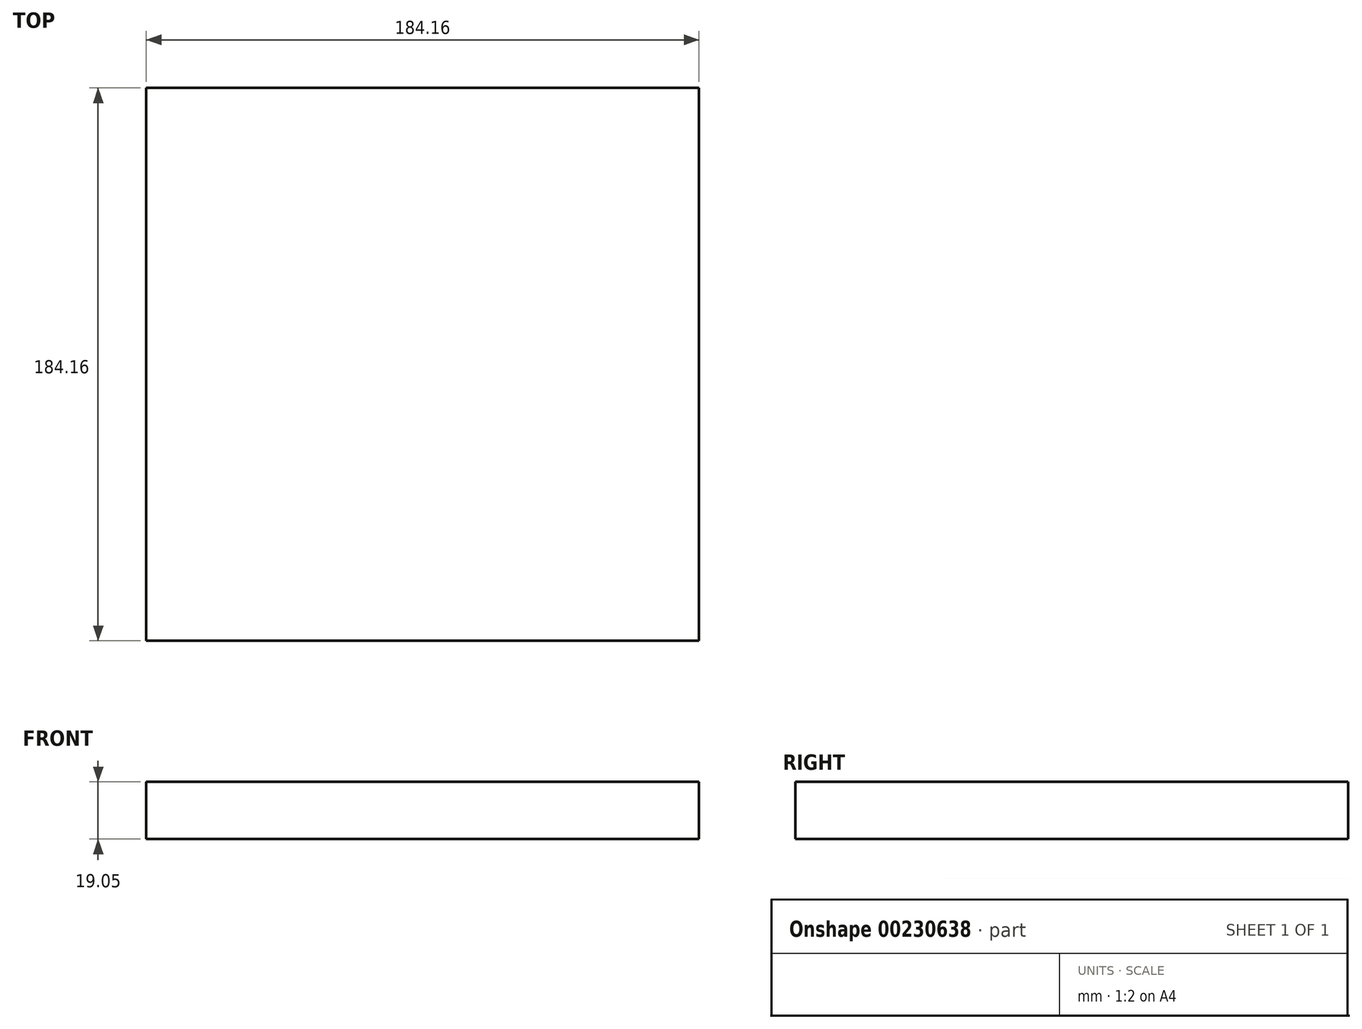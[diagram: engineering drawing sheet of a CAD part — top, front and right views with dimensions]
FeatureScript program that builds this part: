
annotation { "Feature Type Name" : "Feature", "Feature Type Description" : "" }
export const myFeature = defineFeature(function(context is Context, id is Id, definition is map)
    precondition{}
    {
        {
            var Q0;
            Q0=qCreatedBy(makeId("Top.planeOp"),FACE);
            var sketch = newSketch(context, id + "F0", { "sketchPlane" : qUnion([Q0])});
            skLineSegment(sketch, "E0.bottom", {"start": v(92.08, 92.08) * mm, "end": v(-92.07, 92.08) * mm});
            skLineSegment(sketch, "E0.top", {"start": v(92.08, -92.08) * mm, "end": v(-92.08, -92.08) * mm});
            skLineSegment(sketch, "E0.left", {"start": v(92.08, 92.07) * mm, "end": v(92.08, -92.08) * mm});
            skLineSegment(sketch, "E0.right", {"start": v(-92.07, 92.08) * mm, "end": v(-92.08, -92.08) * mm});
            skPoint(sketch, "E0.middle", {"position": v(0, 0) * mm});
            skSolve(sketch);
        }
        {
            var Q0;
            Q0 = qSketchRegion(id + "F0", true);
            extrude(context, id + "F1", {"entities" : qUnion([Q0]), "depth" : 19.05 * mm});
        }
    });
